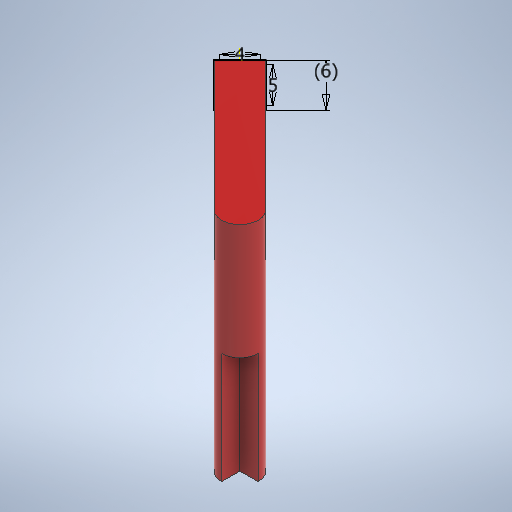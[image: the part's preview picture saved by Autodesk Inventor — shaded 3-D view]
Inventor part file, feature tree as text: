
AUTODESK INVENTOR PART (.ipt)
format: ipt  version: 2025.1 (Build 291241000, 241)  size: 293,888 bytes
history: native  units: in
note: dims shown in document units (in); Inventor stores cm internally (conversion verified against a paired STEP export)
features: sketch x4, extrude x3, other x1
ambient origin geometry x8: Origin, YZ Plane, XZ Plane, XY Plane, X Axis, Y Axis, Z Axis, Center Point
bodies: Solid1 (feature_tree)
feature tree (8):
  extrude  "Extrusion1"  Depth=1.0in TaperAngle=0.0deg
  extrude  "Extrusion2"  TaperAngle=135.0deg  [1 undecoded]
  sketch  "Sketch3"  dims[d5=0.2362in d6=0.0in d7=0.1575in]
  extrude  "Extrusion4"  Depth=0.2362in
  sketch  "Sketch1"  dims[d0=0.2in d1=1.0in d2=0.0in]
  sketch  "Sketch2"  dims[d3=1.0in d4=135.0deg]
  sketch  "Sketch5"  dims[d8=0.1969in d11=0.2362in d12=0.6299in d13=0.0in]
  other  "Finish1"
note: 1 required parameter value undecoded (feature->parameter linkage not recoverable at this tier; creation-order binding heuristic only, values carry confidence <= 0.55)
